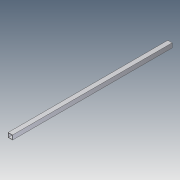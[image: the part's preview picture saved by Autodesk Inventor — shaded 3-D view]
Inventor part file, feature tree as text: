
AUTODESK INVENTOR PART (.ipt)
format: ipt  version: 2012 (Build 160160000, 160)  size: 71,680 bytes
history: native  units: in
note: dims shown in document units (in); Inventor stores cm internally (conversion verified against a paired STEP export)
features: extrude x1, sketch x1
ambient origin geometry x8: Origin, YZ Plane, XZ Plane, XY Plane, X Axis, Y Axis, Z Axis, Center Point
bodies: Solid1 (feature_tree)
feature tree (2):
  extrude  "Extrusion1"  Depth=1.25in
  sketch  "Sketch1"  dims[d0=0.125in d1=1.25in d2=45.5in d3=0.0in]
